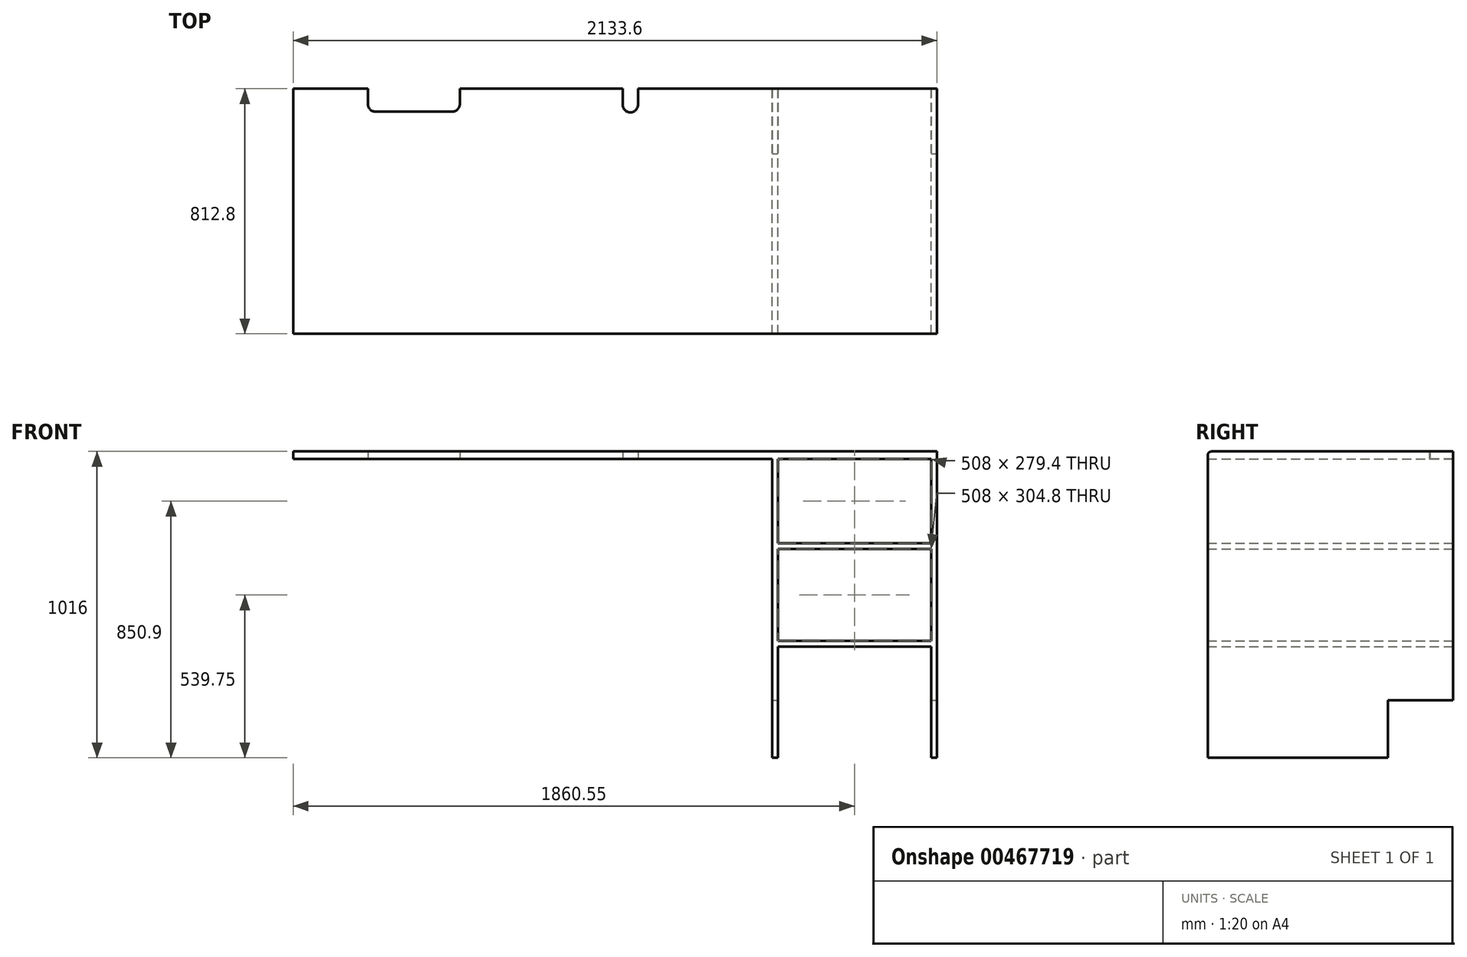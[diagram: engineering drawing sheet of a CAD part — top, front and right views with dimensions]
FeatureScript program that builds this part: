
annotation { "Feature Type Name" : "Feature", "Feature Type Description" : "" }
export const myFeature = defineFeature(function(context is Context, id is Id, definition is map)
    precondition{}
    {
        {
            var Q0;
            Q0=qCreatedBy(makeId("Top.planeOp"),FACE);
            var sketch = newSketch(context, id + "F0", { "sketchPlane" : qUnion([Q0])});
            skLineSegment(sketch, "E0.bottom", {"start": v(-1066.8, 406.4) * mm, "end": v(1066.8, 406.4) * mm});
            skLineSegment(sketch, "E0.top", {"start": v(-1066.8, -406.4) * mm, "end": v(1066.8, -406.4) * mm});
            skLineSegment(sketch, "E0.left", {"start": v(-1066.8, 406.4) * mm, "end": v(-1066.8, -406.4) * mm});
            skLineSegment(sketch, "E0.right", {"start": v(1066.8, 406.4) * mm, "end": v(1066.8, -406.4) * mm});
            skPoint(sketch, "E0.middle", {"position": v(0, 0) * mm});
            skLineSegment(sketch, "E1.bottom", {"start": v(-819.15, 406.4) * mm, "end": v(-514.35, 406.4) * mm});
            skLineSegment(sketch, "E1.top", {"start": v(-793.75, 330.2) * mm, "end": v(-539.75, 330.2) * mm});
            skLineSegment(sketch, "E1.left", {"start": v(-819.15, 406.4) * mm, "end": v(-819.15, 355.6) * mm});
            skLineSegment(sketch, "E1.right", {"start": v(-514.35, 406.4) * mm, "end": v(-514.35, 355.6) * mm});
            skLineSegment(sketch, "E2.bottom", {"start": v(25.4, 406.4) * mm, "end": v(76.2, 406.4) * mm});
            skLineSegment(sketch, "E2.top", {"start": v(50.8, 328.08) * mm, "end": v(50.8, 328.08) * mm});
            skLineSegment(sketch, "E2.left", {"start": v(25.4, 406.4) * mm, "end": v(25.4, 353.48) * mm});
            skLineSegment(sketch, "E2.right", {"start": v(76.2, 406.4) * mm, "end": v(76.2, 353.48) * mm});
            skPoint(sketch, "E3.visualSharp", {"position": v(-819.15, 330.2) * mm});
            skArc(sketch, "E3.filletArc", {"start": v(-819.15, 355.6) * mm, "mid": v(-811.71, 337.64) * mm, "end": v(-793.75, 330.2) * mm});
            skPoint(sketch, "E4.visualSharp", {"position": v(-514.35, 330.2) * mm});
            skArc(sketch, "E4.filletArc", {"start": v(-539.75, 330.2) * mm, "mid": v(-521.79, 337.64) * mm, "end": v(-514.35, 355.6) * mm});
            skPoint(sketch, "E5.visualSharp", {"position": v(25.4, 328.08) * mm});
            skArc(sketch, "E5.filletArc", {"start": v(25.4, 353.48) * mm, "mid": v(32.84, 335.52) * mm, "end": v(50.8, 328.08) * mm});
            skPoint(sketch, "E6.visualSharp", {"position": v(76.2, 328.08) * mm});
            skArc(sketch, "E6.filletArc", {"start": v(50.8, 328.08) * mm, "mid": v(68.76, 335.52) * mm, "end": v(76.2, 353.48) * mm});
            skSolve(sketch);
        }
        {
            var Q0;
            Q0=makeQuery(id+"F0.imprint","IMPRINT",FACE,{"disambiguationData":[TD([[makeQuery(id+"F0.imprint","IMPRINT",EDGE,{"derivedFrom":sQuery(id+"F0.wireOp",EDGE,"E0.top")}),1.0]])]});
            extrude(context, id + "F1", {"entities" : qUnion([Q0]), "depth" : 25.4 * mm});
        }
        {
            var Q0;
            Q0=makeQuery(id+"F1.opExtrude","CAP_EDGE",EDGE,{"disambiguationData":[OSD([sQuery(id+"F0.wireOp",EDGE,"E0.top")])],"isStart":false});
            fillet(context, id + "F2", {"entities" : qUnion([Q0]), "radius" : 12.7 * mm, "tangentPropagation" : true, "allowEdgeOverflow" : false});
        }
        {
            var Q0;
            Q0=qCreatedBy(makeId("Front.planeOp"),FACE);
            var sketch = newSketch(context, id + "F3", { "sketchPlane" : qUnion([Q0])});
            skLineSegment(sketch, "E7.bottom", {"start": v(1066.8, 0) * mm, "end": v(1047.75, 0) * mm});
            skLineSegment(sketch, "E7.top", {"start": v(1066.8, -990.6) * mm, "end": v(1047.75, -990.6) * mm});
            skLineSegment(sketch, "E7.left", {"start": v(1066.8, 0) * mm, "end": v(1066.8, -990.6) * mm});
            skLineSegment(sketch, "E7.right", {"start": v(1047.75, 0) * mm, "end": v(1047.75, -990.6) * mm});
            skLineSegment(sketch, "E8.bottom", {"start": v(539.75, 0) * mm, "end": v(520.7, 0) * mm});
            skLineSegment(sketch, "E8.top", {"start": v(539.75, -990.6) * mm, "end": v(520.7, -990.6) * mm});
            skLineSegment(sketch, "E8.left", {"start": v(539.75, 0) * mm, "end": v(539.75, -990.6) * mm});
            skLineSegment(sketch, "E8.right", {"start": v(520.7, 0) * mm, "end": v(520.7, -990.6) * mm});
            skLineSegment(sketch, "E9.bottom", {"start": v(539.75, -279.4) * mm, "end": v(1047.75, -279.4) * mm});
            skLineSegment(sketch, "E9.top", {"start": v(539.75, -298.45) * mm, "end": v(1047.75, -298.45) * mm});
            skLineSegment(sketch, "E9.left", {"start": v(539.75, -279.4) * mm, "end": v(539.75, -298.45) * mm});
            skLineSegment(sketch, "E9.right", {"start": v(1047.75, -279.4) * mm, "end": v(1047.75, -298.45) * mm});
            skLineSegment(sketch, "E10.bottom", {"start": v(539.75, -603.25) * mm, "end": v(1047.75, -603.25) * mm});
            skLineSegment(sketch, "E10.top", {"start": v(539.75, -622.3) * mm, "end": v(1047.75, -622.3) * mm});
            skLineSegment(sketch, "E10.left", {"start": v(539.75, -603.25) * mm, "end": v(539.75, -622.3) * mm});
            skLineSegment(sketch, "E10.right", {"start": v(1047.75, -603.25) * mm, "end": v(1047.75, -622.3) * mm});
            skSolve(sketch);
        }
        {
            var Q0;
            Q0=makeQuery(id+"F3.imprint","IMPRINT",FACE,{"disambiguationData":[TD([[makeQuery(id+"F3.imprint","IMPRINT",EDGE,{"derivedFrom":sQuery(id+"F3.wireOp",EDGE,"E7.bottom")}),1.0]])]});
            var Q1;
            {var subQ3=sQuery(id+"F3.wireOp",EDGE,"E8.bottom");Q1=makeQuery(id+"F3.imprint","IMPRINT",FACE,{"disambiguationData":[TD([[makeQuery(id+"F3.imprint","IMPRINT",EDGE,{"derivedFrom":subQ3}),1.0]])]});}
            var Q2;
            Q2=makeQuery(id+"F3.imprint","IMPRINT",FACE,{"disambiguationData":[TD([[makeQuery(id+"F3.imprint","IMPRINT",EDGE,{"derivedFrom":sQuery(id+"F3.wireOp",EDGE,"E9.bottom")}),-1.0]])]});
            var Q3;
            Q3=makeQuery(id+"F3.imprint","IMPRINT",FACE,{"disambiguationData":[TD([[makeQuery(id+"F3.imprint","IMPRINT",EDGE,{"derivedFrom":sQuery(id+"F3.wireOp",EDGE,"E10.bottom")}),-1.0]])]});
            var Q4;
            Q4=sQuery(id+"F3.wireOp",EDGE,"E7.right");
            extrude(context, id + "F4", {"entities" : qUnion([Q0, Q1, Q2, Q3]), "operationType" : NewBodyOperationType.ADD, "surfaceEntities" : qUnion([Q4]), "depth" : 406.4 * mm, "hasSecondDirection" : true, "secondDirectionOppositeDirection" : true, "secondDirectionDepth" : 406.4 * mm});
        }
        {
            var Q0;
            Q0=makeQuery(id+"F4.boolean.opBoolean","MERGE",FACE,{"derivedFrom":[makeQuery(id+"F1.opExtrude","SWEPT_FACE",FACE,{"disambiguationData":[OSD([sQuery(id+"F0.wireOp",EDGE,"E0.right")])]}),makeQuery(id+"F4.opExtrude","SWEPT_FACE",FACE,{"disambiguationData":[OSD([sQuery(id+"F3.wireOp",EDGE,"E7.left")])]})]});
            var sketch = newSketch(context, id + "F5", { "sketchPlane" : qUnion([Q0])});
            skLineSegment(sketch, "E11.bottom", {"start": v(406.4, -990.6) * mm, "end": v(190.5, -990.6) * mm});
            skLineSegment(sketch, "E11.top", {"start": v(406.4, -800.1) * mm, "end": v(190.5, -800.1) * mm});
            skLineSegment(sketch, "E11.left", {"start": v(406.4, -990.6) * mm, "end": v(406.4, -800.1) * mm});
            skLineSegment(sketch, "E11.right", {"start": v(190.5, -990.6) * mm, "end": v(190.5, -800.1) * mm});
            skSolve(sketch);
        }
        {
            var Q0;
            Q0=makeQuery(id+"F5.imprint","IMPRINT",FACE,{"disambiguationData":[TD([[makeQuery(id+"F5.imprint","IMPRINT",EDGE,{"derivedFrom":sQuery(id+"F5.wireOp",EDGE,"E11.bottom")}),1.0]])]});
            extrude(context, id + "F6", {"entities" : qUnion([Q0]), "operationType" : NewBodyOperationType.REMOVE, "endBound" : BoundingType.THROUGH_ALL, "oppositeDirection" : true, "depth" : 25.4 * mm});
        }
    });
